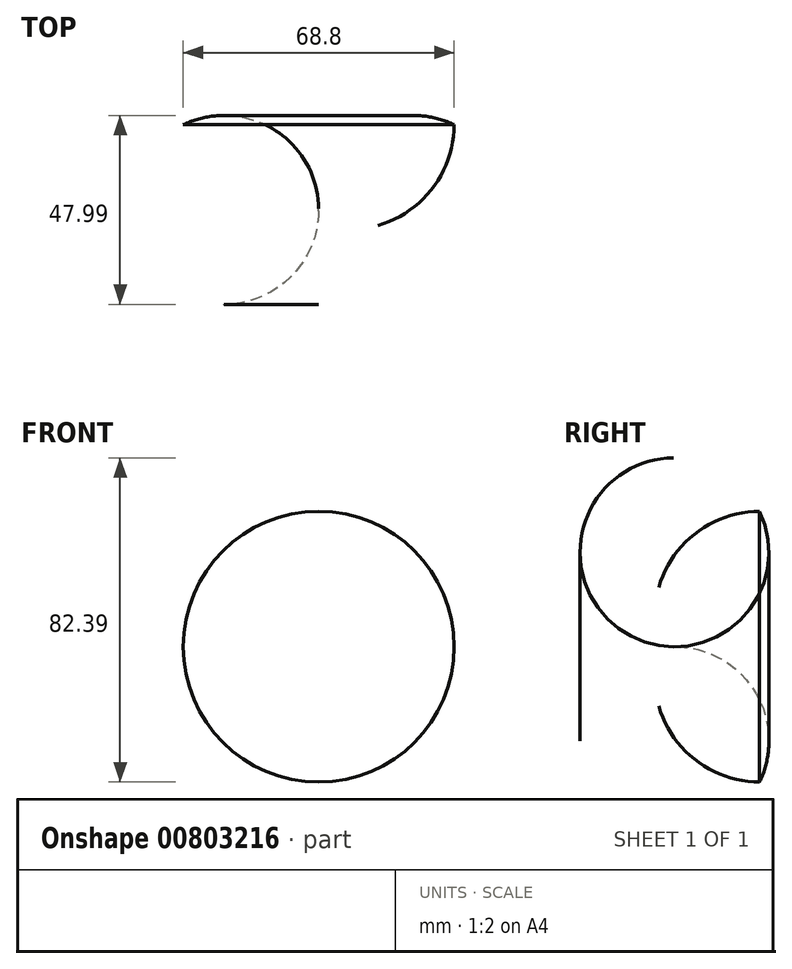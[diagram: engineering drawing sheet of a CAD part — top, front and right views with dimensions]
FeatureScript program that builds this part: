
annotation { "Feature Type Name" : "Feature", "Feature Type Description" : "" }
export const myFeature = defineFeature(function(context is Context, id is Id, definition is map)
    precondition{}
    {
        {
            var Q0;
            Q0=qCreatedBy(makeId("Top.planeOp"),FACE);
            var sketch = newSketch(context, id + "F0", { "sketchPlane" : qUnion([Q0])});
            skLineSegment(sketch, "E0", {"start": v(0, 74.83) * mm, "end": v(0, -73.91) * mm, "construction": true});
            skArc(sketch, "E1", {"start": v(34.4, 0) * mm, "mid": v(11.1, -1.38) * mm, "end": v(0, -21.9) * mm});
            skArc(sketch, "E2", {"start": v(34.4, 0) * mm, "mid": v(23.7, 21.6) * mm, "end": v(0, 25.92) * mm});
            skLineSegment(sketch, "E3", {"start": v(0, 25.92) * mm, "end": v(0, -21.9) * mm});
            skSolve(sketch);
        }
        {
            var Q0;
            {var subQ0=sQuery(id+"F0.wireOp",EDGE,"E2");Q0=makeQuery(id+"F0.imprint","IMPRINT",FACE,{"disambiguationData":[TD([[makeQuery(id+"F0.imprint","IMPRINT",EDGE,{"derivedFrom":subQ0}),1.0]])]});}
            var Q1;
            Q1=sQuery(id+"F0.wireOp",EDGE,"E0");
            revolve(context, id + "F1", {"surfaceOperationType" : NewSurfaceOperationType.NEW, "entities" : qUnion([Q0]), "axis" : qUnion([Q1]), "revolveType" : RevolveType.FULL});
        }
    });
